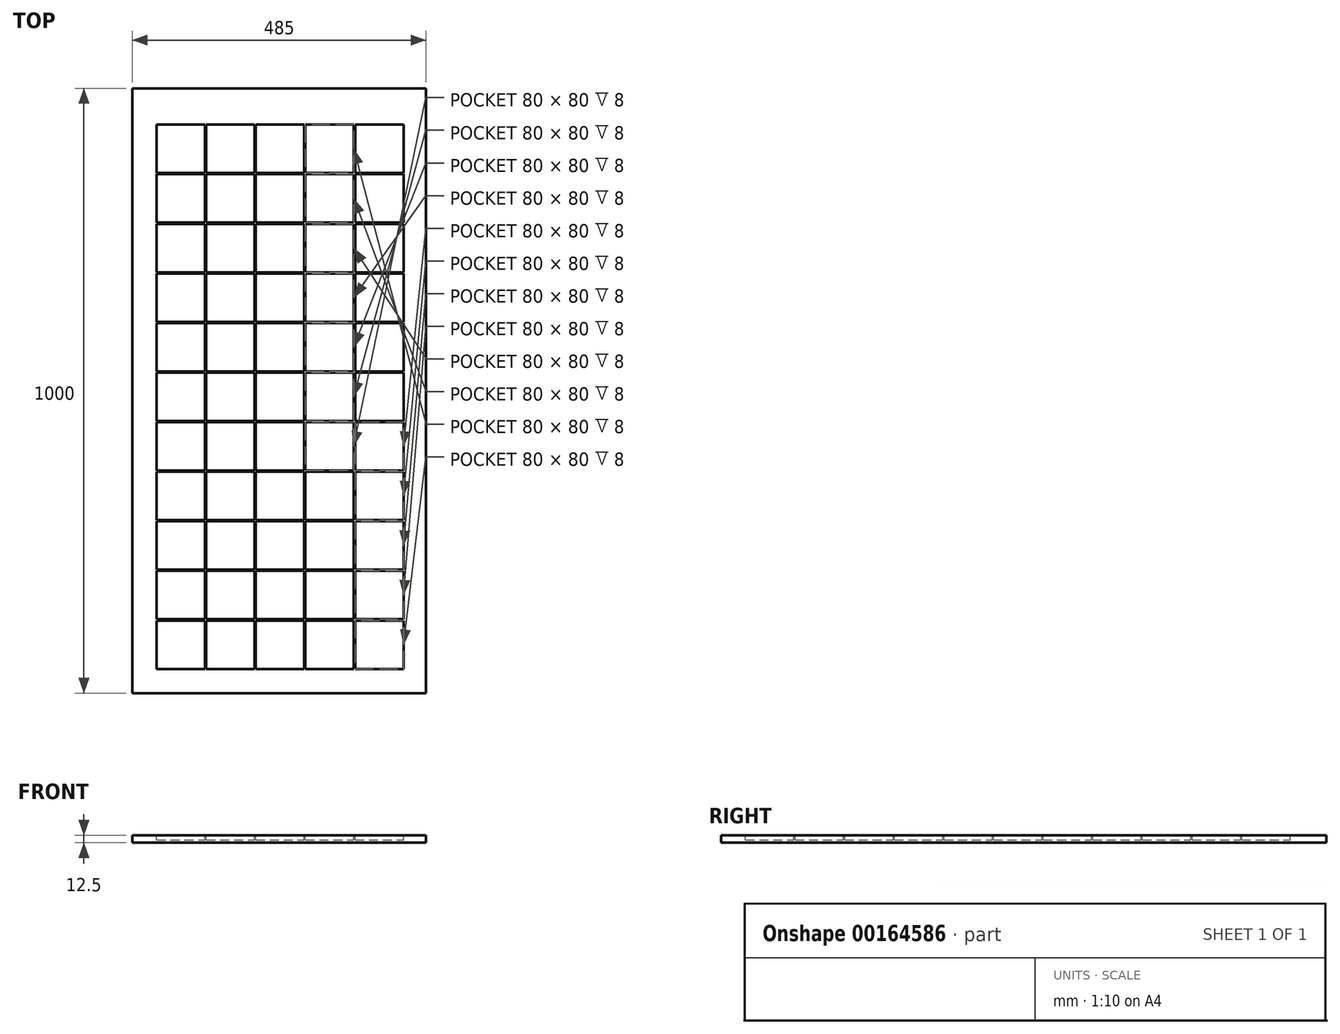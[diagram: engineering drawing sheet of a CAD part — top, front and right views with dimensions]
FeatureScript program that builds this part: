
annotation { "Feature Type Name" : "Feature", "Feature Type Description" : "" }
export const myFeature = defineFeature(function(context is Context, id is Id, definition is map)
    precondition{}
    {
        {
            var Q0;
            Q0=qCreatedBy(makeId("Top.planeOp"),FACE);
            var sketch = newSketch(context, id + "F0", { "sketchPlane" : qUnion([Q0])});
            skLineSegment(sketch, "E0.bottom", {"start": v(-450.89, 950.8) * mm, "end": v(34.11, 950.8) * mm});
            skLineSegment(sketch, "E0.top", {"start": v(-450.89, -49.2) * mm, "end": v(34.11, -49.2) * mm});
            skLineSegment(sketch, "E0.left", {"start": v(-450.89, 950.8) * mm, "end": v(-450.89, -49.2) * mm});
            skLineSegment(sketch, "E0.right", {"start": v(34.11, 950.8) * mm, "end": v(34.11, -49.2) * mm});
            skSolve(sketch);
        }
        {
            var Q0;
            Q0 = qSketchRegion(id + "F0", true);
            extrude(context, id + "F1", {"entities" : qUnion([Q0]), "depth" : 12.5 * mm});
        }
        {
            assignVariable(context, id + "F2", {"variableType" : VariableType.LENGTH, "name" : "Tray_depth", "lengthValue" : 8 * mm});
        }
        {
            var Q0;
            Q0=makeQuery(id+"F1.opExtrude","CAP_FACE",FACE,{"disambiguationData":[OSD([sQuery(id+"F0.wireOp",EDGE,"E0.bottom"),sQuery(id+"F0.wireOp",EDGE,"E0.top"),sQuery(id+"F0.wireOp",EDGE,"E0.left"),sQuery(id+"F0.wireOp",EDGE,"E0.right")])],"isStart":false});
            var sketch = newSketch(context, id + "F3", { "sketchPlane" : qUnion([Q0])});
            skLineSegment(sketch, "E1.bottom", {"start": v(-410.89, -9.2) * mm, "end": v(-330.89, -9.2) * mm});
            skLineSegment(sketch, "E1.top", {"start": v(-410.89, 70.8) * mm, "end": v(-330.89, 70.8) * mm});
            skLineSegment(sketch, "E1.left", {"start": v(-410.89, -9.2) * mm, "end": v(-410.89, 70.8) * mm});
            skLineSegment(sketch, "E1.right", {"start": v(-330.89, -9.2) * mm, "end": v(-330.89, 70.8) * mm});
            skLineSegment(sketch, "E2.0.1.0", {"start": v(-410.89, 72.8) * mm, "end": v(-410.89, 152.8) * mm});
            skLineSegment(sketch, "E2.0.1.1", {"start": v(-330.89, 72.8) * mm, "end": v(-330.89, 152.8) * mm});
            skLineSegment(sketch, "E2.0.1.2", {"start": v(-410.89, 152.8) * mm, "end": v(-330.89, 152.8) * mm});
            skLineSegment(sketch, "E2.0.1.3", {"start": v(-410.89, 72.8) * mm, "end": v(-330.89, 72.8) * mm});
            skLineSegment(sketch, "E2.0.2.0", {"start": v(-410.89, 154.8) * mm, "end": v(-410.89, 234.8) * mm});
            skLineSegment(sketch, "E2.0.2.1", {"start": v(-330.89, 154.8) * mm, "end": v(-330.89, 234.8) * mm});
            skLineSegment(sketch, "E2.0.2.2", {"start": v(-410.89, 234.8) * mm, "end": v(-330.89, 234.8) * mm});
            skLineSegment(sketch, "E2.0.2.3", {"start": v(-410.89, 154.8) * mm, "end": v(-330.89, 154.8) * mm});
            skLineSegment(sketch, "E2.0.3.0", {"start": v(-410.89, 236.8) * mm, "end": v(-410.89, 316.8) * mm});
            skLineSegment(sketch, "E2.0.3.1", {"start": v(-330.89, 236.8) * mm, "end": v(-330.89, 316.8) * mm});
            skLineSegment(sketch, "E2.0.3.2", {"start": v(-410.89, 316.8) * mm, "end": v(-330.89, 316.8) * mm});
            skLineSegment(sketch, "E2.0.3.3", {"start": v(-410.89, 236.8) * mm, "end": v(-330.89, 236.8) * mm});
            skLineSegment(sketch, "E2.0.4.0", {"start": v(-410.89, 318.8) * mm, "end": v(-410.89, 398.8) * mm});
            skLineSegment(sketch, "E2.0.4.1", {"start": v(-330.89, 318.8) * mm, "end": v(-330.89, 398.8) * mm});
            skLineSegment(sketch, "E2.0.4.2", {"start": v(-410.89, 398.8) * mm, "end": v(-330.89, 398.8) * mm});
            skLineSegment(sketch, "E2.0.4.3", {"start": v(-410.89, 318.8) * mm, "end": v(-330.89, 318.8) * mm});
            skLineSegment(sketch, "E2.0.5.0", {"start": v(-410.89, 400.8) * mm, "end": v(-410.89, 480.8) * mm});
            skLineSegment(sketch, "E2.0.5.1", {"start": v(-330.89, 400.8) * mm, "end": v(-330.89, 480.8) * mm});
            skLineSegment(sketch, "E2.0.5.2", {"start": v(-410.89, 480.8) * mm, "end": v(-330.89, 480.8) * mm});
            skLineSegment(sketch, "E2.0.5.3", {"start": v(-410.89, 400.8) * mm, "end": v(-330.89, 400.8) * mm});
            skLineSegment(sketch, "E2.0.6.0", {"start": v(-410.89, 482.8) * mm, "end": v(-410.89, 562.8) * mm});
            skLineSegment(sketch, "E2.0.6.1", {"start": v(-330.89, 482.8) * mm, "end": v(-330.89, 562.8) * mm});
            skLineSegment(sketch, "E2.0.6.2", {"start": v(-410.89, 562.8) * mm, "end": v(-330.89, 562.8) * mm});
            skLineSegment(sketch, "E2.0.6.3", {"start": v(-410.89, 482.8) * mm, "end": v(-330.89, 482.8) * mm});
            skLineSegment(sketch, "E2.0.7.0", {"start": v(-410.89, 564.8) * mm, "end": v(-410.89, 644.8) * mm});
            skLineSegment(sketch, "E2.0.7.1", {"start": v(-330.89, 564.8) * mm, "end": v(-330.89, 644.8) * mm});
            skLineSegment(sketch, "E2.0.7.2", {"start": v(-410.89, 644.8) * mm, "end": v(-330.89, 644.8) * mm});
            skLineSegment(sketch, "E2.0.7.3", {"start": v(-410.89, 564.8) * mm, "end": v(-330.89, 564.8) * mm});
            skLineSegment(sketch, "E2.0.8.0", {"start": v(-410.89, 646.8) * mm, "end": v(-410.89, 726.8) * mm});
            skLineSegment(sketch, "E2.0.8.1", {"start": v(-330.89, 646.8) * mm, "end": v(-330.89, 726.8) * mm});
            skLineSegment(sketch, "E2.0.8.2", {"start": v(-410.89, 726.8) * mm, "end": v(-330.89, 726.8) * mm});
            skLineSegment(sketch, "E2.0.8.3", {"start": v(-410.89, 646.8) * mm, "end": v(-330.89, 646.8) * mm});
            skLineSegment(sketch, "E2.0.9.0", {"start": v(-410.89, 728.8) * mm, "end": v(-410.89, 808.8) * mm});
            skLineSegment(sketch, "E2.0.9.1", {"start": v(-330.89, 728.8) * mm, "end": v(-330.89, 808.8) * mm});
            skLineSegment(sketch, "E2.0.9.2", {"start": v(-410.89, 808.8) * mm, "end": v(-330.89, 808.8) * mm});
            skLineSegment(sketch, "E2.0.9.3", {"start": v(-410.89, 728.8) * mm, "end": v(-330.89, 728.8) * mm});
            skLineSegment(sketch, "E2.0.10.0", {"start": v(-410.89, 810.8) * mm, "end": v(-410.89, 890.8) * mm});
            skLineSegment(sketch, "E2.0.10.1", {"start": v(-330.89, 810.8) * mm, "end": v(-330.89, 890.8) * mm});
            skLineSegment(sketch, "E2.0.10.2", {"start": v(-410.89, 890.8) * mm, "end": v(-330.89, 890.8) * mm});
            skLineSegment(sketch, "E2.0.10.3", {"start": v(-410.89, 810.8) * mm, "end": v(-330.89, 810.8) * mm});
            skLineSegment(sketch, "E2.1.0.0", {"start": v(-328.89, -9.2) * mm, "end": v(-328.89, 70.8) * mm});
            skLineSegment(sketch, "E2.1.0.1", {"start": v(-248.89, -9.2) * mm, "end": v(-248.89, 70.8) * mm});
            skLineSegment(sketch, "E2.1.0.2", {"start": v(-328.89, 70.8) * mm, "end": v(-248.89, 70.8) * mm});
            skLineSegment(sketch, "E2.1.0.3", {"start": v(-328.89, -9.2) * mm, "end": v(-248.89, -9.2) * mm});
            skLineSegment(sketch, "E2.1.1.0", {"start": v(-328.89, 72.8) * mm, "end": v(-328.89, 152.8) * mm});
            skLineSegment(sketch, "E2.1.1.1", {"start": v(-248.89, 72.8) * mm, "end": v(-248.89, 152.8) * mm});
            skLineSegment(sketch, "E2.1.1.2", {"start": v(-328.89, 152.8) * mm, "end": v(-248.89, 152.8) * mm});
            skLineSegment(sketch, "E2.1.1.3", {"start": v(-328.89, 72.8) * mm, "end": v(-248.89, 72.8) * mm});
            skLineSegment(sketch, "E2.1.2.0", {"start": v(-328.89, 154.8) * mm, "end": v(-328.89, 234.8) * mm});
            skLineSegment(sketch, "E2.1.2.1", {"start": v(-248.89, 154.8) * mm, "end": v(-248.89, 234.8) * mm});
            skLineSegment(sketch, "E2.1.2.2", {"start": v(-328.89, 234.8) * mm, "end": v(-248.89, 234.8) * mm});
            skLineSegment(sketch, "E2.1.2.3", {"start": v(-328.89, 154.8) * mm, "end": v(-248.89, 154.8) * mm});
            skLineSegment(sketch, "E2.1.3.0", {"start": v(-328.89, 236.8) * mm, "end": v(-328.89, 316.8) * mm});
            skLineSegment(sketch, "E2.1.3.1", {"start": v(-248.89, 236.8) * mm, "end": v(-248.89, 316.8) * mm});
            skLineSegment(sketch, "E2.1.3.2", {"start": v(-328.89, 316.8) * mm, "end": v(-248.89, 316.8) * mm});
            skLineSegment(sketch, "E2.1.3.3", {"start": v(-328.89, 236.8) * mm, "end": v(-248.89, 236.8) * mm});
            skLineSegment(sketch, "E2.1.4.0", {"start": v(-328.89, 318.8) * mm, "end": v(-328.89, 398.8) * mm});
            skLineSegment(sketch, "E2.1.4.1", {"start": v(-248.89, 318.8) * mm, "end": v(-248.89, 398.8) * mm});
            skLineSegment(sketch, "E2.1.4.2", {"start": v(-328.89, 398.8) * mm, "end": v(-248.89, 398.8) * mm});
            skLineSegment(sketch, "E2.1.4.3", {"start": v(-328.89, 318.8) * mm, "end": v(-248.89, 318.8) * mm});
            skLineSegment(sketch, "E2.1.5.0", {"start": v(-328.89, 400.8) * mm, "end": v(-328.89, 480.8) * mm});
            skLineSegment(sketch, "E2.1.5.1", {"start": v(-248.89, 400.8) * mm, "end": v(-248.89, 480.8) * mm});
            skLineSegment(sketch, "E2.1.5.2", {"start": v(-328.89, 480.8) * mm, "end": v(-248.89, 480.8) * mm});
            skLineSegment(sketch, "E2.1.5.3", {"start": v(-328.89, 400.8) * mm, "end": v(-248.89, 400.8) * mm});
            skLineSegment(sketch, "E2.1.6.0", {"start": v(-328.89, 482.8) * mm, "end": v(-328.89, 562.8) * mm});
            skLineSegment(sketch, "E2.1.6.1", {"start": v(-248.89, 482.8) * mm, "end": v(-248.89, 562.8) * mm});
            skLineSegment(sketch, "E2.1.6.2", {"start": v(-328.89, 562.8) * mm, "end": v(-248.89, 562.8) * mm});
            skLineSegment(sketch, "E2.1.6.3", {"start": v(-328.89, 482.8) * mm, "end": v(-248.89, 482.8) * mm});
            skLineSegment(sketch, "E2.1.7.0", {"start": v(-328.89, 564.8) * mm, "end": v(-328.89, 644.8) * mm});
            skLineSegment(sketch, "E2.1.7.1", {"start": v(-248.89, 564.8) * mm, "end": v(-248.89, 644.8) * mm});
            skLineSegment(sketch, "E2.1.7.2", {"start": v(-328.89, 644.8) * mm, "end": v(-248.89, 644.8) * mm});
            skLineSegment(sketch, "E2.1.7.3", {"start": v(-328.89, 564.8) * mm, "end": v(-248.89, 564.8) * mm});
            skLineSegment(sketch, "E2.1.8.0", {"start": v(-328.89, 646.8) * mm, "end": v(-328.89, 726.8) * mm});
            skLineSegment(sketch, "E2.1.8.1", {"start": v(-248.89, 646.8) * mm, "end": v(-248.89, 726.8) * mm});
            skLineSegment(sketch, "E2.1.8.2", {"start": v(-328.89, 726.8) * mm, "end": v(-248.89, 726.8) * mm});
            skLineSegment(sketch, "E2.1.8.3", {"start": v(-328.89, 646.8) * mm, "end": v(-248.89, 646.8) * mm});
            skLineSegment(sketch, "E2.1.9.0", {"start": v(-328.89, 728.8) * mm, "end": v(-328.89, 808.8) * mm});
            skLineSegment(sketch, "E2.1.9.1", {"start": v(-248.89, 728.8) * mm, "end": v(-248.89, 808.8) * mm});
            skLineSegment(sketch, "E2.1.9.2", {"start": v(-328.89, 808.8) * mm, "end": v(-248.89, 808.8) * mm});
            skLineSegment(sketch, "E2.1.9.3", {"start": v(-328.89, 728.8) * mm, "end": v(-248.89, 728.8) * mm});
            skLineSegment(sketch, "E2.1.10.0", {"start": v(-328.89, 810.8) * mm, "end": v(-328.89, 890.8) * mm});
            skLineSegment(sketch, "E2.1.10.1", {"start": v(-248.89, 810.8) * mm, "end": v(-248.89, 890.8) * mm});
            skLineSegment(sketch, "E2.1.10.2", {"start": v(-328.89, 890.8) * mm, "end": v(-248.89, 890.8) * mm});
            skLineSegment(sketch, "E2.1.10.3", {"start": v(-328.89, 810.8) * mm, "end": v(-248.89, 810.8) * mm});
            skLineSegment(sketch, "E2.2.0.0", {"start": v(-246.89, -9.2) * mm, "end": v(-246.89, 70.8) * mm});
            skLineSegment(sketch, "E2.2.0.1", {"start": v(-166.89, -9.2) * mm, "end": v(-166.89, 70.8) * mm});
            skLineSegment(sketch, "E2.2.0.2", {"start": v(-246.89, 70.8) * mm, "end": v(-166.89, 70.8) * mm});
            skLineSegment(sketch, "E2.2.0.3", {"start": v(-246.89, -9.2) * mm, "end": v(-166.89, -9.2) * mm});
            skLineSegment(sketch, "E2.2.1.0", {"start": v(-246.89, 72.8) * mm, "end": v(-246.89, 152.8) * mm});
            skLineSegment(sketch, "E2.2.1.1", {"start": v(-166.89, 72.8) * mm, "end": v(-166.89, 152.8) * mm});
            skLineSegment(sketch, "E2.2.1.2", {"start": v(-246.89, 152.8) * mm, "end": v(-166.89, 152.8) * mm});
            skLineSegment(sketch, "E2.2.1.3", {"start": v(-246.89, 72.8) * mm, "end": v(-166.89, 72.8) * mm});
            skLineSegment(sketch, "E2.2.2.0", {"start": v(-246.89, 154.8) * mm, "end": v(-246.89, 234.8) * mm});
            skLineSegment(sketch, "E2.2.2.1", {"start": v(-166.89, 154.8) * mm, "end": v(-166.89, 234.8) * mm});
            skLineSegment(sketch, "E2.2.2.2", {"start": v(-246.89, 234.8) * mm, "end": v(-166.89, 234.8) * mm});
            skLineSegment(sketch, "E2.2.2.3", {"start": v(-246.89, 154.8) * mm, "end": v(-166.89, 154.8) * mm});
            skLineSegment(sketch, "E2.2.3.0", {"start": v(-246.89, 236.8) * mm, "end": v(-246.89, 316.8) * mm});
            skLineSegment(sketch, "E2.2.3.1", {"start": v(-166.89, 236.8) * mm, "end": v(-166.89, 316.8) * mm});
            skLineSegment(sketch, "E2.2.3.2", {"start": v(-246.89, 316.8) * mm, "end": v(-166.89, 316.8) * mm});
            skLineSegment(sketch, "E2.2.3.3", {"start": v(-246.89, 236.8) * mm, "end": v(-166.89, 236.8) * mm});
            skLineSegment(sketch, "E2.2.4.0", {"start": v(-246.89, 318.8) * mm, "end": v(-246.89, 398.8) * mm});
            skLineSegment(sketch, "E2.2.4.1", {"start": v(-166.89, 318.8) * mm, "end": v(-166.89, 398.8) * mm});
            skLineSegment(sketch, "E2.2.4.2", {"start": v(-246.89, 398.8) * mm, "end": v(-166.89, 398.8) * mm});
            skLineSegment(sketch, "E2.2.4.3", {"start": v(-246.89, 318.8) * mm, "end": v(-166.89, 318.8) * mm});
            skLineSegment(sketch, "E2.2.5.0", {"start": v(-246.89, 400.8) * mm, "end": v(-246.89, 480.8) * mm});
            skLineSegment(sketch, "E2.2.5.1", {"start": v(-166.89, 400.8) * mm, "end": v(-166.89, 480.8) * mm});
            skLineSegment(sketch, "E2.2.5.2", {"start": v(-246.89, 480.8) * mm, "end": v(-166.89, 480.8) * mm});
            skLineSegment(sketch, "E2.2.5.3", {"start": v(-246.89, 400.8) * mm, "end": v(-166.89, 400.8) * mm});
            skLineSegment(sketch, "E2.2.6.0", {"start": v(-246.89, 482.8) * mm, "end": v(-246.89, 562.8) * mm});
            skLineSegment(sketch, "E2.2.6.1", {"start": v(-166.89, 482.8) * mm, "end": v(-166.89, 562.8) * mm});
            skLineSegment(sketch, "E2.2.6.2", {"start": v(-246.89, 562.8) * mm, "end": v(-166.89, 562.8) * mm});
            skLineSegment(sketch, "E2.2.6.3", {"start": v(-246.89, 482.8) * mm, "end": v(-166.89, 482.8) * mm});
            skLineSegment(sketch, "E2.2.7.0", {"start": v(-246.89, 564.8) * mm, "end": v(-246.89, 644.8) * mm});
            skLineSegment(sketch, "E2.2.7.1", {"start": v(-166.89, 564.8) * mm, "end": v(-166.89, 644.8) * mm});
            skLineSegment(sketch, "E2.2.7.2", {"start": v(-246.89, 644.8) * mm, "end": v(-166.89, 644.8) * mm});
            skLineSegment(sketch, "E2.2.7.3", {"start": v(-246.89, 564.8) * mm, "end": v(-166.89, 564.8) * mm});
            skLineSegment(sketch, "E2.2.8.0", {"start": v(-246.89, 646.8) * mm, "end": v(-246.89, 726.8) * mm});
            skLineSegment(sketch, "E2.2.8.1", {"start": v(-166.89, 646.8) * mm, "end": v(-166.89, 726.8) * mm});
            skLineSegment(sketch, "E2.2.8.2", {"start": v(-246.89, 726.8) * mm, "end": v(-166.89, 726.8) * mm});
            skLineSegment(sketch, "E2.2.8.3", {"start": v(-246.89, 646.8) * mm, "end": v(-166.89, 646.8) * mm});
            skLineSegment(sketch, "E2.2.9.0", {"start": v(-246.89, 728.8) * mm, "end": v(-246.89, 808.8) * mm});
            skLineSegment(sketch, "E2.2.9.1", {"start": v(-166.89, 728.8) * mm, "end": v(-166.89, 808.8) * mm});
            skLineSegment(sketch, "E2.2.9.2", {"start": v(-246.89, 808.8) * mm, "end": v(-166.89, 808.8) * mm});
            skLineSegment(sketch, "E2.2.9.3", {"start": v(-246.89, 728.8) * mm, "end": v(-166.89, 728.8) * mm});
            skLineSegment(sketch, "E2.2.10.0", {"start": v(-246.89, 810.8) * mm, "end": v(-246.89, 890.8) * mm});
            skLineSegment(sketch, "E2.2.10.1", {"start": v(-166.89, 810.8) * mm, "end": v(-166.89, 890.8) * mm});
            skLineSegment(sketch, "E2.2.10.2", {"start": v(-246.89, 890.8) * mm, "end": v(-166.89, 890.8) * mm});
            skLineSegment(sketch, "E2.2.10.3", {"start": v(-246.89, 810.8) * mm, "end": v(-166.89, 810.8) * mm});
            skLineSegment(sketch, "E2.3.0.0", {"start": v(-164.89, -9.2) * mm, "end": v(-164.89, 70.8) * mm});
            skLineSegment(sketch, "E2.3.0.1", {"start": v(-84.89, -9.2) * mm, "end": v(-84.89, 70.8) * mm});
            skLineSegment(sketch, "E2.3.0.2", {"start": v(-164.89, 70.8) * mm, "end": v(-84.89, 70.8) * mm});
            skLineSegment(sketch, "E2.3.0.3", {"start": v(-164.89, -9.2) * mm, "end": v(-84.89, -9.2) * mm});
            skLineSegment(sketch, "E2.3.1.0", {"start": v(-164.89, 72.8) * mm, "end": v(-164.89, 152.8) * mm});
            skLineSegment(sketch, "E2.3.1.1", {"start": v(-84.89, 72.8) * mm, "end": v(-84.89, 152.8) * mm});
            skLineSegment(sketch, "E2.3.1.2", {"start": v(-164.89, 152.8) * mm, "end": v(-84.89, 152.8) * mm});
            skLineSegment(sketch, "E2.3.1.3", {"start": v(-164.89, 72.8) * mm, "end": v(-84.89, 72.8) * mm});
            skLineSegment(sketch, "E2.3.2.0", {"start": v(-164.89, 154.8) * mm, "end": v(-164.89, 234.8) * mm});
            skLineSegment(sketch, "E2.3.2.1", {"start": v(-84.89, 154.8) * mm, "end": v(-84.89, 234.8) * mm});
            skLineSegment(sketch, "E2.3.2.2", {"start": v(-164.89, 234.8) * mm, "end": v(-84.89, 234.8) * mm});
            skLineSegment(sketch, "E2.3.2.3", {"start": v(-164.89, 154.8) * mm, "end": v(-84.89, 154.8) * mm});
            skLineSegment(sketch, "E2.3.3.0", {"start": v(-164.89, 236.8) * mm, "end": v(-164.89, 316.8) * mm});
            skLineSegment(sketch, "E2.3.3.1", {"start": v(-84.89, 236.8) * mm, "end": v(-84.89, 316.8) * mm});
            skLineSegment(sketch, "E2.3.3.2", {"start": v(-164.89, 316.8) * mm, "end": v(-84.89, 316.8) * mm});
            skLineSegment(sketch, "E2.3.3.3", {"start": v(-164.89, 236.8) * mm, "end": v(-84.89, 236.8) * mm});
            skLineSegment(sketch, "E2.3.4.0", {"start": v(-164.89, 318.8) * mm, "end": v(-164.89, 398.8) * mm});
            skLineSegment(sketch, "E2.3.4.1", {"start": v(-84.89, 318.8) * mm, "end": v(-84.89, 398.8) * mm});
            skLineSegment(sketch, "E2.3.4.2", {"start": v(-164.89, 398.8) * mm, "end": v(-84.89, 398.8) * mm});
            skLineSegment(sketch, "E2.3.4.3", {"start": v(-164.89, 318.8) * mm, "end": v(-84.89, 318.8) * mm});
            skLineSegment(sketch, "E2.3.5.0", {"start": v(-164.89, 400.8) * mm, "end": v(-164.89, 480.8) * mm});
            skLineSegment(sketch, "E2.3.5.1", {"start": v(-84.89, 400.8) * mm, "end": v(-84.89, 480.8) * mm});
            skLineSegment(sketch, "E2.3.5.2", {"start": v(-164.89, 480.8) * mm, "end": v(-84.89, 480.8) * mm});
            skLineSegment(sketch, "E2.3.5.3", {"start": v(-164.89, 400.8) * mm, "end": v(-84.89, 400.8) * mm});
            skLineSegment(sketch, "E2.3.6.0", {"start": v(-164.89, 482.8) * mm, "end": v(-164.89, 562.8) * mm});
            skLineSegment(sketch, "E2.3.6.1", {"start": v(-84.89, 482.8) * mm, "end": v(-84.89, 562.8) * mm});
            skLineSegment(sketch, "E2.3.6.2", {"start": v(-164.89, 562.8) * mm, "end": v(-84.89, 562.8) * mm});
            skLineSegment(sketch, "E2.3.6.3", {"start": v(-164.89, 482.8) * mm, "end": v(-84.89, 482.8) * mm});
            skLineSegment(sketch, "E2.3.7.0", {"start": v(-164.89, 564.8) * mm, "end": v(-164.89, 644.8) * mm});
            skLineSegment(sketch, "E2.3.7.1", {"start": v(-84.89, 564.8) * mm, "end": v(-84.89, 644.8) * mm});
            skLineSegment(sketch, "E2.3.7.2", {"start": v(-164.89, 644.8) * mm, "end": v(-84.89, 644.8) * mm});
            skLineSegment(sketch, "E2.3.7.3", {"start": v(-164.89, 564.8) * mm, "end": v(-84.89, 564.8) * mm});
            skLineSegment(sketch, "E2.3.8.0", {"start": v(-164.89, 646.8) * mm, "end": v(-164.89, 726.8) * mm});
            skLineSegment(sketch, "E2.3.8.1", {"start": v(-84.89, 646.8) * mm, "end": v(-84.89, 726.8) * mm});
            skLineSegment(sketch, "E2.3.8.2", {"start": v(-164.89, 726.8) * mm, "end": v(-84.89, 726.8) * mm});
            skLineSegment(sketch, "E2.3.8.3", {"start": v(-164.89, 646.8) * mm, "end": v(-84.89, 646.8) * mm});
            skLineSegment(sketch, "E2.3.9.0", {"start": v(-164.89, 728.8) * mm, "end": v(-164.89, 808.8) * mm});
            skLineSegment(sketch, "E2.3.9.1", {"start": v(-84.89, 728.8) * mm, "end": v(-84.89, 808.8) * mm});
            skLineSegment(sketch, "E2.3.9.2", {"start": v(-164.89, 808.8) * mm, "end": v(-84.89, 808.8) * mm});
            skLineSegment(sketch, "E2.3.9.3", {"start": v(-164.89, 728.8) * mm, "end": v(-84.89, 728.8) * mm});
            skLineSegment(sketch, "E2.3.10.0", {"start": v(-164.89, 810.8) * mm, "end": v(-164.89, 890.8) * mm});
            skLineSegment(sketch, "E2.3.10.1", {"start": v(-84.89, 810.8) * mm, "end": v(-84.89, 890.8) * mm});
            skLineSegment(sketch, "E2.3.10.2", {"start": v(-164.89, 890.8) * mm, "end": v(-84.89, 890.8) * mm});
            skLineSegment(sketch, "E2.3.10.3", {"start": v(-164.89, 810.8) * mm, "end": v(-84.89, 810.8) * mm});
            skLineSegment(sketch, "E2.4.0.0", {"start": v(-82.89, -9.2) * mm, "end": v(-82.89, 70.8) * mm});
            skLineSegment(sketch, "E2.4.0.1", {"start": v(-2.89, -9.2) * mm, "end": v(-2.89, 70.8) * mm});
            skLineSegment(sketch, "E2.4.0.2", {"start": v(-82.89, 70.8) * mm, "end": v(-2.89, 70.8) * mm});
            skLineSegment(sketch, "E2.4.0.3", {"start": v(-82.89, -9.2) * mm, "end": v(-2.89, -9.2) * mm});
            skLineSegment(sketch, "E2.4.1.0", {"start": v(-82.89, 72.8) * mm, "end": v(-82.89, 152.8) * mm});
            skLineSegment(sketch, "E2.4.1.1", {"start": v(-2.89, 72.8) * mm, "end": v(-2.89, 152.8) * mm});
            skLineSegment(sketch, "E2.4.1.2", {"start": v(-82.89, 152.8) * mm, "end": v(-2.89, 152.8) * mm});
            skLineSegment(sketch, "E2.4.1.3", {"start": v(-82.89, 72.8) * mm, "end": v(-2.89, 72.8) * mm});
            skLineSegment(sketch, "E2.4.2.0", {"start": v(-82.89, 154.8) * mm, "end": v(-82.89, 234.8) * mm});
            skLineSegment(sketch, "E2.4.2.1", {"start": v(-2.89, 154.8) * mm, "end": v(-2.89, 234.8) * mm});
            skLineSegment(sketch, "E2.4.2.2", {"start": v(-82.89, 234.8) * mm, "end": v(-2.89, 234.8) * mm});
            skLineSegment(sketch, "E2.4.2.3", {"start": v(-82.89, 154.8) * mm, "end": v(-2.89, 154.8) * mm});
            skLineSegment(sketch, "E2.4.3.0", {"start": v(-82.89, 236.8) * mm, "end": v(-82.89, 316.8) * mm});
            skLineSegment(sketch, "E2.4.3.1", {"start": v(-2.89, 236.8) * mm, "end": v(-2.89, 316.8) * mm});
            skLineSegment(sketch, "E2.4.3.2", {"start": v(-82.89, 316.8) * mm, "end": v(-2.89, 316.8) * mm});
            skLineSegment(sketch, "E2.4.3.3", {"start": v(-82.89, 236.8) * mm, "end": v(-2.89, 236.8) * mm});
            skLineSegment(sketch, "E2.4.4.0", {"start": v(-82.89, 318.8) * mm, "end": v(-82.89, 398.8) * mm});
            skLineSegment(sketch, "E2.4.4.1", {"start": v(-2.89, 318.8) * mm, "end": v(-2.89, 398.8) * mm});
            skLineSegment(sketch, "E2.4.4.2", {"start": v(-82.89, 398.8) * mm, "end": v(-2.89, 398.8) * mm});
            skLineSegment(sketch, "E2.4.4.3", {"start": v(-82.89, 318.8) * mm, "end": v(-2.89, 318.8) * mm});
            skLineSegment(sketch, "E2.4.5.0", {"start": v(-82.89, 400.8) * mm, "end": v(-82.89, 480.8) * mm});
            skLineSegment(sketch, "E2.4.5.1", {"start": v(-2.89, 400.8) * mm, "end": v(-2.89, 480.8) * mm});
            skLineSegment(sketch, "E2.4.5.2", {"start": v(-82.89, 480.8) * mm, "end": v(-2.89, 480.8) * mm});
            skLineSegment(sketch, "E2.4.5.3", {"start": v(-82.89, 400.8) * mm, "end": v(-2.89, 400.8) * mm});
            skLineSegment(sketch, "E2.4.6.0", {"start": v(-82.89, 482.8) * mm, "end": v(-82.89, 562.8) * mm});
            skLineSegment(sketch, "E2.4.6.1", {"start": v(-2.89, 482.8) * mm, "end": v(-2.89, 562.8) * mm});
            skLineSegment(sketch, "E2.4.6.2", {"start": v(-82.89, 562.8) * mm, "end": v(-2.89, 562.8) * mm});
            skLineSegment(sketch, "E2.4.6.3", {"start": v(-82.89, 482.8) * mm, "end": v(-2.89, 482.8) * mm});
            skLineSegment(sketch, "E2.4.7.0", {"start": v(-82.89, 564.8) * mm, "end": v(-82.89, 644.8) * mm});
            skLineSegment(sketch, "E2.4.7.1", {"start": v(-2.89, 564.8) * mm, "end": v(-2.89, 644.8) * mm});
            skLineSegment(sketch, "E2.4.7.2", {"start": v(-82.89, 644.8) * mm, "end": v(-2.89, 644.8) * mm});
            skLineSegment(sketch, "E2.4.7.3", {"start": v(-82.89, 564.8) * mm, "end": v(-2.89, 564.8) * mm});
            skLineSegment(sketch, "E2.4.8.0", {"start": v(-82.89, 646.8) * mm, "end": v(-82.89, 726.8) * mm});
            skLineSegment(sketch, "E2.4.8.1", {"start": v(-2.89, 646.8) * mm, "end": v(-2.89, 726.8) * mm});
            skLineSegment(sketch, "E2.4.8.2", {"start": v(-82.89, 726.8) * mm, "end": v(-2.89, 726.8) * mm});
            skLineSegment(sketch, "E2.4.8.3", {"start": v(-82.89, 646.8) * mm, "end": v(-2.89, 646.8) * mm});
            skLineSegment(sketch, "E2.4.9.0", {"start": v(-82.89, 728.8) * mm, "end": v(-82.89, 808.8) * mm});
            skLineSegment(sketch, "E2.4.9.1", {"start": v(-2.89, 728.8) * mm, "end": v(-2.89, 808.8) * mm});
            skLineSegment(sketch, "E2.4.9.2", {"start": v(-82.89, 808.8) * mm, "end": v(-2.89, 808.8) * mm});
            skLineSegment(sketch, "E2.4.9.3", {"start": v(-82.89, 728.8) * mm, "end": v(-2.89, 728.8) * mm});
            skLineSegment(sketch, "E2.4.10.0", {"start": v(-82.89, 810.8) * mm, "end": v(-82.89, 890.8) * mm});
            skLineSegment(sketch, "E2.4.10.1", {"start": v(-2.89, 810.8) * mm, "end": v(-2.89, 890.8) * mm});
            skLineSegment(sketch, "E2.4.10.2", {"start": v(-82.89, 890.8) * mm, "end": v(-2.89, 890.8) * mm});
            skLineSegment(sketch, "E2.4.10.3", {"start": v(-82.89, 810.8) * mm, "end": v(-2.89, 810.8) * mm});
            skLineSegment(sketch, "E2.direction1", {"start": v(-410.89, -9.2) * mm, "end": v(-328.89, -9.2) * mm, "construction": true});
            skLineSegment(sketch, "E2.direction2", {"start": v(-410.89, -9.2) * mm, "end": v(-410.89, 72.8) * mm, "construction": true});
            skSolve(sketch);
        }
        {
            var Q0;
            Q0 = qSketchRegion(id + "F3", true);
            extrude(context, id + "F4", {"entities" : qUnion([Q0]), "operationType" : NewBodyOperationType.REMOVE, "oppositeDirection" : true, "depth" : getVariable(context, 'Tray_depth'), "offsetDistance" : 25 * mm});
        }
    });
